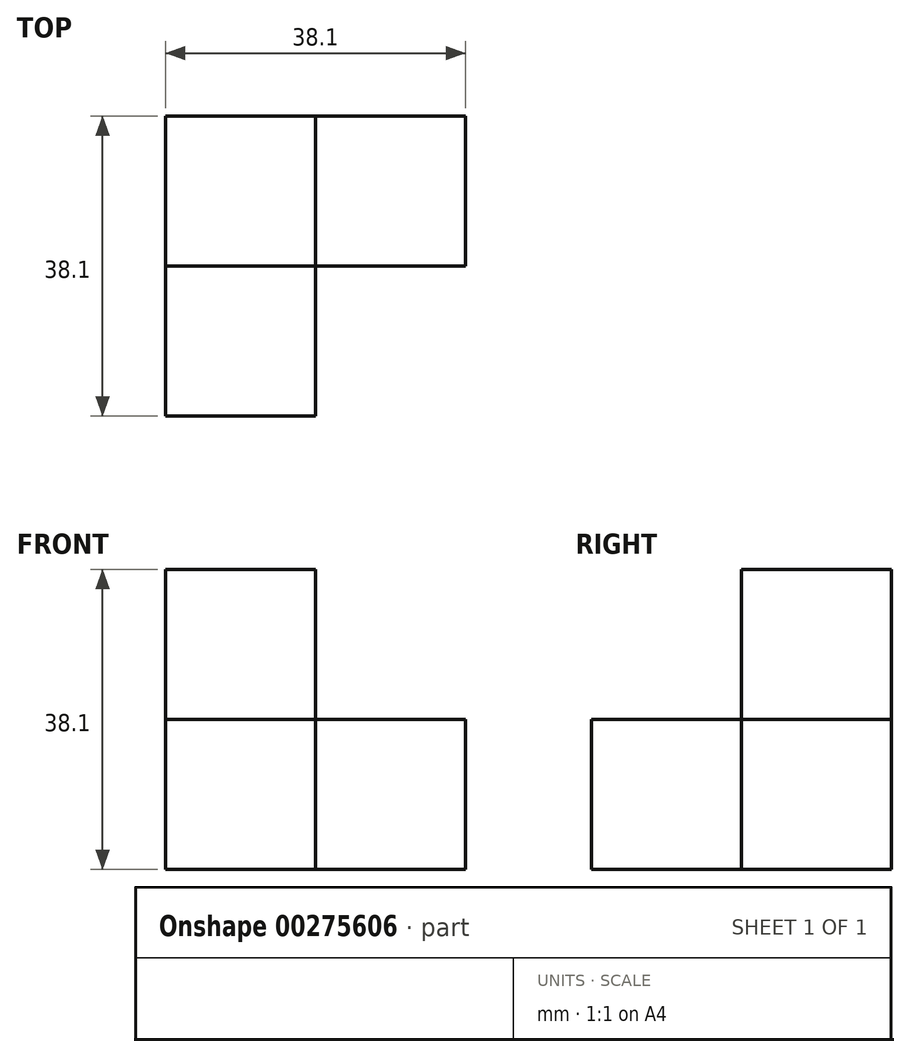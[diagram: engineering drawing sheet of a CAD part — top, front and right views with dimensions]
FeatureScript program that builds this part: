
annotation { "Feature Type Name" : "Feature", "Feature Type Description" : "" }
export const myFeature = defineFeature(function(context is Context, id is Id, definition is map)
    precondition{}
    {
        {
            var Q0;
            Q0=qCreatedBy(makeId("Top.planeOp"),FACE);
            var sketch = newSketch(context, id + "F0", { "sketchPlane" : qUnion([Q0])});
            skLineSegment(sketch, "E0.bottom", {"start": v(-20.9, 33.05) * mm, "end": v(-1.85, 33.05) * mm});
            skLineSegment(sketch, "E0.top", {"start": v(-20.9, 14) * mm, "end": v(-1.85, 14) * mm});
            skLineSegment(sketch, "E0.left", {"start": v(-20.9, 33.05) * mm, "end": v(-20.9, 14) * mm});
            skLineSegment(sketch, "E0.right", {"start": v(-1.85, 33.05) * mm, "end": v(-1.85, 14) * mm});
            skLineSegment(sketch, "E1.bottom", {"start": v(-1.85, 33.05) * mm, "end": v(17.2, 33.05) * mm});
            skLineSegment(sketch, "E1.top", {"start": v(-1.85, 14) * mm, "end": v(17.2, 14) * mm});
            skLineSegment(sketch, "E1.right", {"start": v(17.2, 33.05) * mm, "end": v(17.2, 14) * mm});
            skLineSegment(sketch, "E2.bottom", {"start": v(17.2, 14) * mm, "end": v(-1.85, 14) * mm});
            skLineSegment(sketch, "E2.top", {"start": v(17.2, -5.05) * mm, "end": v(-1.85, -5.05) * mm});
            skLineSegment(sketch, "E2.left", {"start": v(17.2, 14) * mm, "end": v(17.2, -5.05) * mm});
            skLineSegment(sketch, "E2.right", {"start": v(-1.85, 14) * mm, "end": v(-1.85, -5.05) * mm});
            skLineSegment(sketch, "E3.bottom", {"start": v(-1.85, -5.05) * mm, "end": v(-20.9, -5.05) * mm});
            skLineSegment(sketch, "E3.top", {"start": v(-1.85, 14) * mm, "end": v(-20.9, 14) * mm});
            skLineSegment(sketch, "E3.left", {"start": v(-1.85, -5.05) * mm, "end": v(-1.85, 14) * mm});
            skLineSegment(sketch, "E3.right", {"start": v(-20.9, -5.05) * mm, "end": v(-20.9, 14) * mm});
            skSolve(sketch);
        }
        {
            var Q0;
            Q0=makeQuery(id+"F0.imprint","IMPRINT",FACE,{"disambiguationData":[TD([[makeQuery(id+"F0.imprint","IMPRINT",EDGE,{"derivedFrom":sQuery(id+"F0.wireOp",EDGE,"E1.bottom")}),-1.0]])]});
            var Q1;
            Q1=makeQuery(id+"F0.imprint","IMPRINT",FACE,{"disambiguationData":[TD([[makeQuery(id+"F0.imprint","IMPRINT",EDGE,{"derivedFrom":sQuery(id+"F0.wireOp",EDGE,"E3.bottom")}),-1.0]])]});
            extrude(context, id + "F1", {"entities" : qUnion([Q0, Q1]), "depth" : 19.05 * mm});
        }
        {
            var Q0;
            Q0=makeQuery(id+"F0.imprint","IMPRINT",FACE,{"disambiguationData":[TD([[makeQuery(id+"F0.imprint","IMPRINT",EDGE,{"derivedFrom":sQuery(id+"F0.wireOp",EDGE,"E0.bottom")}),-1.0]])]});
            var Q1;
            Q1=makeQuery(id+"F0.imprint","IMPRINT",FACE,{"disambiguationData":[TD([[makeQuery(id+"F0.imprint","IMPRINT",EDGE,{"derivedFrom":sQuery(id+"F0.wireOp",EDGE,"E2.bottom")}),1.0]])]});
            extrude(context, id + "F2", {"entities" : qUnion([Q0, Q1]), "depth" : 38.1 * mm});
        }
    });
